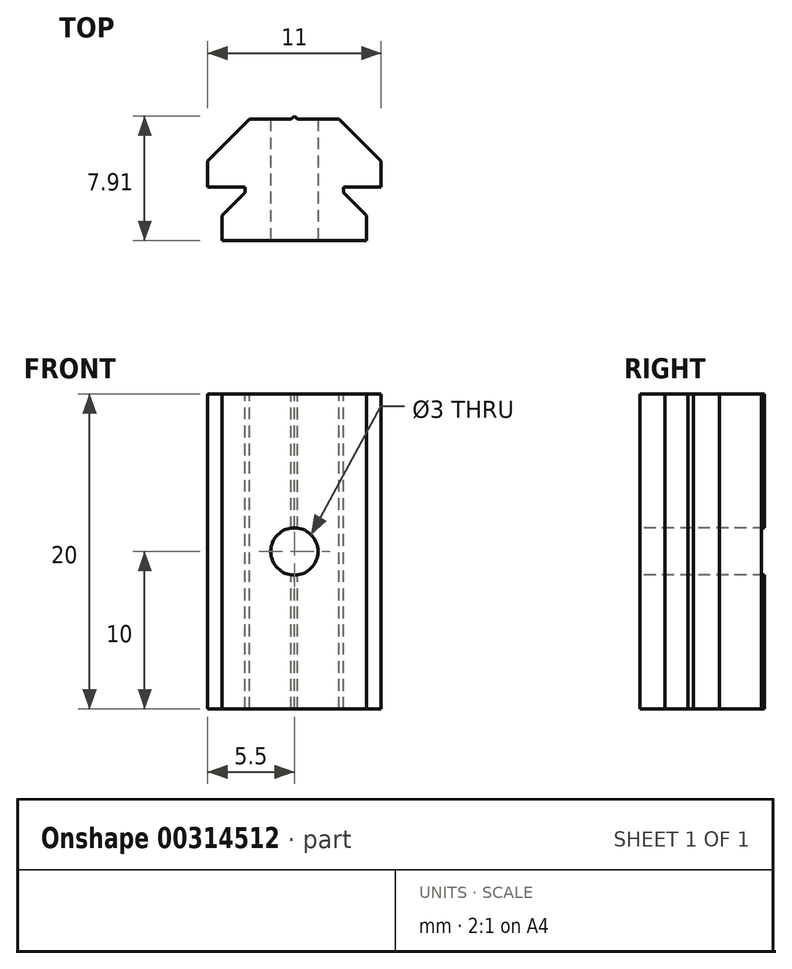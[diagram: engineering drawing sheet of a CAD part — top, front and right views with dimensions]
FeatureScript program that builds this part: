
annotation { "Feature Type Name" : "Feature", "Feature Type Description" : "" }
export const myFeature = defineFeature(function(context is Context, id is Id, definition is map)
    precondition{}
    {
        {
            var Q0;
            Q0=qCreatedBy(makeId("Top.planeOp"),FACE);
            var sketch = newSketch(context, id + "F0", { "sketchPlane" : qUnion([Q0])});
            skLineSegment(sketch, "E0.0.0", {"start": v(3.7, -4.4) * mm, "end": v(3.9, -4.61) * mm});
            skLineSegment(sketch, "E0.0.1", {"start": v(3.9, -4.61) * mm, "end": v(3.9, -7.24) * mm});
            skLineSegment(sketch, "E0.0.2", {"start": v(3.9, -7.24) * mm, "end": v(6.56, -9.9) * mm});
            skLineSegment(sketch, "E0.0.3", {"start": v(6.56, -9.9) * mm, "end": v(8.2, -9.9) * mm});
            skLineSegment(sketch, "E0.0.4", {"start": v(8.2, -9.9) * mm, "end": v(8.2, -7.53) * mm});
            skLineSegment(sketch, "E0.0.5", {"start": v(8.2, -7.53) * mm, "end": v(8.55, -7.53) * mm});
            skLineSegment(sketch, "E0.0.6", {"start": v(8.55, -7.53) * mm, "end": v(10, -8.98) * mm});
            skLineSegment(sketch, "E0.0.7", {"start": v(10, -8.98) * mm, "end": v(10, -13.9) * mm});
            skArc(sketch, "E0.0.8", {"start": v(10, -13.9) * mm, "mid": v(9.85, -14.25) * mm, "end": v(9.5, -14.4) * mm});
            skLineSegment(sketch, "E0.0.9", {"start": v(9.5, -14.4) * mm, "end": v(4.58, -14.4) * mm});
            skLineSegment(sketch, "E0.0.10", {"start": v(4.58, -14.4) * mm, "end": v(3.12, -12.95) * mm});
            skLineSegment(sketch, "E0.0.11", {"start": v(3.12, -12.95) * mm, "end": v(3.12, -12.6) * mm});
            skLineSegment(sketch, "E0.0.12", {"start": v(3.12, -12.6) * mm, "end": v(5.5, -12.6) * mm});
            skLineSegment(sketch, "E0.0.13", {"start": v(5.5, -12.6) * mm, "end": v(5.5, -10.96) * mm});
            skLineSegment(sketch, "E0.0.14", {"start": v(5.5, -10.96) * mm, "end": v(2.84, -8.3) * mm});
            skLineSegment(sketch, "E0.0.15", {"start": v(2.84, -8.3) * mm, "end": v(0.2, -8.3) * mm});
            skLineSegment(sketch, "E0.0.16", {"start": v(0.2, -8.3) * mm, "end": v(0, -8.1) * mm});
            skLineSegment(sketch, "E0.0.17", {"start": v(0, -8.1) * mm, "end": v(-0.2, -8.3) * mm});
            skLineSegment(sketch, "E0.0.18", {"start": v(-0.2, -8.3) * mm, "end": v(-2.84, -8.3) * mm});
            skLineSegment(sketch, "E0.0.19", {"start": v(-2.84, -8.3) * mm, "end": v(-5.5, -10.96) * mm});
            skLineSegment(sketch, "E0.0.20", {"start": v(-5.5, -10.96) * mm, "end": v(-5.5, -12.6) * mm});
            skLineSegment(sketch, "E0.0.21", {"start": v(-5.5, -12.6) * mm, "end": v(-3.12, -12.6) * mm});
            skLineSegment(sketch, "E0.0.22", {"start": v(-3.12, -12.6) * mm, "end": v(-3.12, -12.95) * mm});
            skLineSegment(sketch, "E0.0.23", {"start": v(-3.12, -12.95) * mm, "end": v(-4.58, -14.4) * mm});
            skLineSegment(sketch, "E0.0.24", {"start": v(-4.58, -14.4) * mm, "end": v(-9.5, -14.4) * mm});
            skArc(sketch, "E0.0.25", {"start": v(-9.5, -14.4) * mm, "mid": v(-9.85, -14.25) * mm, "end": v(-10, -13.9) * mm});
            skLineSegment(sketch, "E0.0.26", {"start": v(-10, -13.9) * mm, "end": v(-10, -8.98) * mm});
            skLineSegment(sketch, "E0.0.27", {"start": v(-10, -8.98) * mm, "end": v(-8.54, -7.53) * mm});
            skLineSegment(sketch, "E0.0.28", {"start": v(-8.54, -7.53) * mm, "end": v(-8.2, -7.53) * mm});
            skLineSegment(sketch, "E0.0.29", {"start": v(-8.2, -7.53) * mm, "end": v(-8.2, -9.9) * mm});
            skLineSegment(sketch, "E0.0.30", {"start": v(-8.2, -9.9) * mm, "end": v(-6.56, -9.9) * mm});
            skLineSegment(sketch, "E0.0.31", {"start": v(-6.56, -9.9) * mm, "end": v(-3.9, -7.24) * mm});
            skLineSegment(sketch, "E0.0.32", {"start": v(-3.9, -7.24) * mm, "end": v(-3.9, -4.6) * mm});
            skLineSegment(sketch, "E0.0.33", {"start": v(-3.9, -4.6) * mm, "end": v(-3.69, -4.4) * mm});
            skLineSegment(sketch, "E0.0.34", {"start": v(-3.69, -4.4) * mm, "end": v(-3.9, -4.2) * mm});
            skLineSegment(sketch, "E0.0.35", {"start": v(-3.9, -4.2) * mm, "end": v(-3.9, -1.56) * mm});
            skLineSegment(sketch, "E0.0.36", {"start": v(-3.9, -1.56) * mm, "end": v(-6.56, 1.1) * mm});
            skLineSegment(sketch, "E0.0.37", {"start": v(-6.56, 1.1) * mm, "end": v(-8.2, 1.1) * mm});
            skLineSegment(sketch, "E0.0.38", {"start": v(-8.2, 1.1) * mm, "end": v(-8.2, -1.28) * mm});
            skLineSegment(sketch, "E0.0.39", {"start": v(-8.2, -1.28) * mm, "end": v(-8.54, -1.28) * mm});
            skLineSegment(sketch, "E0.0.40", {"start": v(-8.54, -1.28) * mm, "end": v(-10, 0.18) * mm});
            skLineSegment(sketch, "E0.0.41", {"start": v(-10, 0.18) * mm, "end": v(-10, 5.1) * mm});
            skArc(sketch, "E0.0.42", {"start": v(-10, 5.1) * mm, "mid": v(-9.85, 5.45) * mm, "end": v(-9.5, 5.6) * mm});
            skLineSegment(sketch, "E0.0.43", {"start": v(-9.5, 5.6) * mm, "end": v(-4.58, 5.6) * mm});
            skLineSegment(sketch, "E0.0.44", {"start": v(-4.58, 5.6) * mm, "end": v(-3.12, 4.14) * mm});
            skLineSegment(sketch, "E0.0.45", {"start": v(-3.12, 4.14) * mm, "end": v(-3.12, 3.8) * mm});
            skLineSegment(sketch, "E0.0.46", {"start": v(-3.12, 3.8) * mm, "end": v(-5.5, 3.8) * mm});
            skLineSegment(sketch, "E0.0.47", {"start": v(-5.5, 3.8) * mm, "end": v(-5.5, 2.16) * mm});
            skLineSegment(sketch, "E0.0.48", {"start": v(-5.5, 2.16) * mm, "end": v(-2.84, -0.5) * mm});
            skLineSegment(sketch, "E0.0.49", {"start": v(-2.84, -0.5) * mm, "end": v(-0.2, -0.5) * mm});
            skLineSegment(sketch, "E0.0.50", {"start": v(-0.2, -0.5) * mm, "end": v(0, -0.71) * mm});
            skLineSegment(sketch, "E0.0.51", {"start": v(0, -0.71) * mm, "end": v(0.21, -0.5) * mm});
            skLineSegment(sketch, "E0.0.52", {"start": v(0.21, -0.5) * mm, "end": v(2.84, -0.5) * mm});
            skLineSegment(sketch, "E0.0.53", {"start": v(2.84, -0.5) * mm, "end": v(5.5, 2.16) * mm});
            skLineSegment(sketch, "E0.0.54", {"start": v(5.5, 2.16) * mm, "end": v(5.5, 3.8) * mm});
            skLineSegment(sketch, "E0.0.55", {"start": v(5.5, 3.8) * mm, "end": v(3.13, 3.8) * mm});
            skLineSegment(sketch, "E0.0.56", {"start": v(3.13, 3.8) * mm, "end": v(3.13, 4.14) * mm});
            skLineSegment(sketch, "E0.0.57", {"start": v(3.13, 4.14) * mm, "end": v(4.58, 5.6) * mm});
            skLineSegment(sketch, "E0.0.58", {"start": v(4.58, 5.6) * mm, "end": v(9.5, 5.6) * mm});
            skArc(sketch, "E0.0.59", {"start": v(9.5, 5.6) * mm, "mid": v(9.85, 5.45) * mm, "end": v(10, 5.1) * mm});
            skLineSegment(sketch, "E0.0.60", {"start": v(10, 5.1) * mm, "end": v(10, 0.18) * mm});
            skLineSegment(sketch, "E0.0.61", {"start": v(10, 0.18) * mm, "end": v(8.55, -1.28) * mm});
            skLineSegment(sketch, "E0.0.62", {"start": v(8.55, -1.28) * mm, "end": v(8.2, -1.28) * mm});
            skLineSegment(sketch, "E0.0.63", {"start": v(8.2, -1.28) * mm, "end": v(8.2, 1.1) * mm});
            skLineSegment(sketch, "E0.0.64", {"start": v(8.2, 1.1) * mm, "end": v(6.56, 1.1) * mm});
            skLineSegment(sketch, "E0.0.65", {"start": v(6.56, 1.1) * mm, "end": v(3.9, -1.56) * mm});
            skLineSegment(sketch, "E0.0.66", {"start": v(3.9, -1.56) * mm, "end": v(3.9, -4.2) * mm});
            skLineSegment(sketch, "E0.0.67", {"start": v(3.9, -4.2) * mm, "end": v(3.7, -4.4) * mm});
            skLineSegment(sketch, "E1", {"start": v(-4.58, -14.4) * mm, "end": v(-4.58, -16) * mm});
            skLineSegment(sketch, "E2", {"start": v(-4.58, -16) * mm, "end": v(4.58, -16) * mm});
            skLineSegment(sketch, "E3", {"start": v(4.58, -16) * mm, "end": v(4.58, -14.4) * mm});
            skSolve(sketch);
        }
        {
            var Q0;
            Q0=makeQuery(id+"F0.imprint","IMPRINT",FACE,{"disambiguationData":[TD([[makeQuery(id+"F0.imprint","IMPRINT",EDGE,{"derivedFrom":sQuery(id+"F0.wireOp",EDGE,"E0.0.10")}),1.0]])]});
            extrude(context, id + "F1", {"entities" : qUnion([Q0]), "oppositeDirection" : true, "depth" : 20 * mm});
        }
        {
            var Q0;
            Q0=makeQuery(id+"F1.opExtrude","SWEPT_FACE",FACE,{"disambiguationData":[OSD([sQuery(id+"F0.wireOp",EDGE,"E2")])]});
            var sketch = newSketch(context, id + "F2", { "sketchPlane" : qUnion([Q0])});
            skCircle(sketch, "E4", {"center": v(0, -10) * mm, "radius": 1.5 * mm});
            skPoint(sketch, "E4.centerSnap0", {"position": v(-4.58, -10) * mm});
            skSolve(sketch);
        }
        {
            var Q0;
            Q0 = qSketchRegion(id + "F2", true);
            extrude(context, id + "F3", {"entities" : qUnion([Q0]), "operationType" : NewBodyOperationType.REMOVE, "oppositeDirection" : true, "depth" : 25 * mm});
        }
    });
